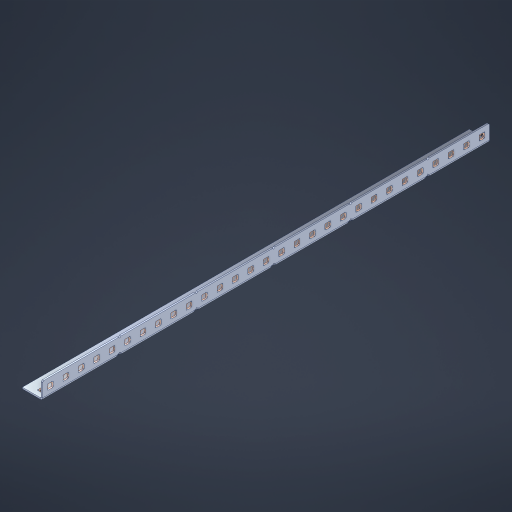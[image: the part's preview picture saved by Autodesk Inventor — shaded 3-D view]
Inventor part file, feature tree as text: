
AUTODESK INVENTOR PART (.ipt)
format: ipt  version: 2023 (Build 270158000, 158)  size: 932,352 bytes
history: native  units: in
note: dims shown in document units (in); Inventor stores cm internally (conversion verified against a paired STEP export)
features: other x63, extrude x57, sheet_metal_op x10, sketch x8, mirror x1, pattern_linear x1, chamfer x1
ambient origin geometry x8: Origin, YZ Plane, XZ Plane, XY Plane, X Axis, Y Axis, Z Axis, Center Point
bodies: Solid1 (feature_tree), Body (feature_tree)
feature tree (141):
  other  "Flange Pattern Plane"
  sheet_metal_op  "Flange Pattern"
  sheet_metal_op  "Body Pattern"
  other  "Arc Length"
  mirror  "Notch Mirror"
  pattern_linear  "Notch Pattern"  Spacing1=0.1875in  [1 undecoded]
  chamfer  "End Chamfer"
  extrude  "Half Cut"  Depth=0.0469in
  sketch  "Sketch1"  dims[d0=2.5in]
  other  "Plate1"
  sketch  "Sketch2"  dims[d1=14.5in]
  other  "Plate2"
  sheet_metal_op  "Bend1"
  sheet_metal_op  "Corner1"
  sketch  "Sketch3"  dims[d2=0.0469in]
  other  "Flange Pattern Sketch"
  sketch  "Sketch7"  dims[d3=0.0469in]
  other  "Srf1"
  other  "Srf2"
  sketch  "Sketch8"  dims[d4=0.0234in]
  sketch  "Sketch9"  dims[d5=0.0938in]
  other  "Srf91"
  sheet_metal_op  "Body Pattern Sketch"
  other  "Srf92"
  sketch  "Sketch13"  dims[d6=0.0469in]
  sketch  "Sketch14"  dims[d7=0.5in d8=90.0deg d9=0.0312in d10=0.1875in d11=0.0469in d12=0.0469in d16=0.182in d17=0.02in d18=0.0469in d19=0.0in d20=0.25in d21=0.25in d46=0.172in d47=1.0in d48=0.0in d49=0.182in d50=0.02in d51=0.25in d52=0.25in d53=0.0469in d54=0.0in d55=0.172in d56=1.0in d57=0.0in d60=11.4173in d62=0.5in d63=0.3937in d65=0.5in d85=0.1227in d86=0.1659in d88=0.04in d89=0.0469in d90=0.0in d91=0.04in d92=0.0491in d95=2.5in d96=0.04in d97=0.25in d98=45.0deg d101=0.0in d102=2.497in d131=0.5in d132=11.4173in d134=0.5in d139=0.5in]
  other  "Srf856"
  other  "Srf1310"
  other  "Srf1311"
  other  "Srf1312"
  other  "Srf1376"
  other  "Srf1377"
  other  "Srf1728"
  other  "Srf1755"
  other  "Srf1878"
  other  "Srf1879"
  other  "Srf1880"
  other  "Srf1881"
  other  "Srf1882"
  other  "Srf1883"
  other  "Srf1884"
  other  "Srf1885"
  other  "Srf1886"
  other  "Srf1887"
  other  "Srf1888"
  other  "Srf1889"
  other  "Srf1890"
  other  "Srf1891"
  other  "Srf1892"
  other  "Srf1893"
  other  "Srf1894"
  other  "Srf1895"
  other  "Srf1896"
  other  "Srf1897"
  other  "Srf1898"
  other  "Srf1899"
  other  "Srf1900"
  other  "Srf1942"
  other  "Srf1943"
  other  "Srf1944"
  other  "Srf1945"
  other  "Srf1946"
  other  "Srf1947"
  other  "Srf1948"
  other  "Srf1949"
  other  "Srf1950"
  other  "Srf1951"
  other  "Srf1952"
  other  "Srf1953"
  other  "Srf1954"
  other  "Srf1955"
  other  "Srf1956"
  other  "Srf1957"
  other  "Srf1958"
  other  "Srf1959"
  other  "Srf1960"
  other  "Srf1961"
  other  "Srf1962"
  other  "Srf1963"
  other  "Srf1964"
  sheet_metal_op  "Flange Stamp"
  sheet_metal_op  "Flange Circle"
  sheet_metal_op  "Body Stamp"
  sheet_metal_op  "Body Circle"
  sheet_metal_op  "Notch"
  extrude  "ExtrusionSrf2"  Depth=0.0469in
  extrude  "ExtrusionSrf92"  Depth=0.5in
  extrude  "ExtrusionSrf856"  Depth=0.02in
  extrude  "ExtrusionSrf1310"  Depth=0.0469in
  extrude  "ExtrusionSrf1311"  TaperAngle=0.0deg  [1 undecoded]
  extrude  "ExtrusionSrf1312"  Depth=0.5in
  extrude  "ExtrusionSrf1376"  Depth=0.5in
  extrude  "ExtrusionSrf1377"  Depth=0.5in
  extrude  "ExtrusionSrf1728"  Depth=0.5in TaperAngle=0.0deg
  extrude  "ExtrusionSrf1755"  Depth=0.5in
  extrude  "ExtrusionSrf1878"  Depth=0.02in
  extrude  "ExtrusionSrf1879"  Depth=0.5in
  extrude  "ExtrusionSrf1880"  Depth=0.5in
  extrude  "ExtrusionSrf1881"  Depth=0.0469in
  extrude  "ExtrusionSrf1882"  TaperAngle=0.0deg  [1 undecoded]
  extrude  "ExtrusionSrf1883"  Depth=0.5in
  extrude  "ExtrusionSrf1884"  Depth=0.5in TaperAngle=0.0deg
  extrude  "ExtrusionSrf1885"  Depth=0.5in
  extrude  "ExtrusionSrf1886"  Depth=0.5in
  extrude  "ExtrusionSrf1887"  Depth=0.5in
  extrude  "ExtrusionSrf1888"  Depth=0.5in
  extrude  "ExtrusionSrf1889"  Depth=0.5in
  extrude  "ExtrusionSrf1890"  Depth=0.0469in
  extrude  "ExtrusionSrf1891"  TaperAngle=0.0deg  [1 undecoded]
  extrude  "ExtrusionSrf1892"  Depth=0.5in
  extrude  "ExtrusionSrf1893"  Depth=0.5in
  extrude  "ExtrusionSrf1894"  Depth=0.5in
  extrude  "ExtrusionSrf1895"  Depth=0.5in TaperAngle=45.0deg
  extrude  "ExtrusionSrf1896"  TaperAngle=0.0deg  [1 undecoded]
  extrude  "ExtrusionSrf1897"  Depth=0.5in
  extrude  "ExtrusionSrf1898"  Depth=0.5in
  extrude  "ExtrusionSrf1899"  Depth=0.5in
  extrude  "ExtrusionSrf1900"  Depth=0.5in
  extrude  "ExtrusionSrf1942"  Depth=0.5in
  extrude  "ExtrusionSrf1943"  [1 undecoded]
  extrude  "ExtrusionSrf1944"  [1 undecoded]
  extrude  "ExtrusionSrf1945"  [1 undecoded]
  extrude  "ExtrusionSrf1946"  [1 undecoded]
  extrude  "ExtrusionSrf1947"  [1 undecoded]
  extrude  "ExtrusionSrf1948"  [1 undecoded]
  extrude  "ExtrusionSrf1949"  [1 undecoded]
  extrude  "ExtrusionSrf1950"  [1 undecoded]
  extrude  "ExtrusionSrf1951"  [1 undecoded]
  extrude  "ExtrusionSrf1952"  [1 undecoded]
  extrude  "ExtrusionSrf1953"  [1 undecoded]
  extrude  "ExtrusionSrf1954"  [1 undecoded]
  extrude  "ExtrusionSrf1955"  [1 undecoded]
  extrude  "ExtrusionSrf1956"  [1 undecoded]
  extrude  "ExtrusionSrf1957"  [1 undecoded]
  extrude  "ExtrusionSrf1958"  [1 undecoded]
  extrude  "ExtrusionSrf1959"  [1 undecoded]
  extrude  "ExtrusionSrf1960"  [1 undecoded]
  extrude  "ExtrusionSrf1961"  [1 undecoded]
  extrude  "ExtrusionSrf1962"  [1 undecoded]
  extrude  "ExtrusionSrf1963"  [1 undecoded]
  extrude  "ExtrusionSrf1964"  [1 undecoded]
note: 27 required parameter values undecoded (feature->parameter linkage not recoverable at this tier; creation-order binding heuristic only, values carry confidence <= 0.55)
